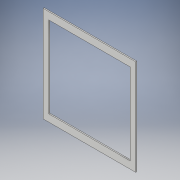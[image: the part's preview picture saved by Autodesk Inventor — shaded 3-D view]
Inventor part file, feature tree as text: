
AUTODESK INVENTOR PART (.ipt)
format: ipt  version: 2017 (Build 210142000, 142)  size: 106,496 bytes
history: native  units: in
note: dims shown in document units (in); Inventor stores cm internally (conversion verified against a paired STEP export)
features: extrude x2, sketch x2
ambient origin geometry x8: Origin, YZ Plane, XZ Plane, XY Plane, X Axis, Y Axis, Z Axis, Center Point
bodies: Solid1 (feature_tree)
feature tree (4):
  extrude  "Extrusion1"  Depth=20.0in
  extrude  "Extrusion2"  Depth=17.0in
  sketch  "Sketch1"  dims[d0=19.333in d1=20.0in]
  sketch  "Sketch2"  dims[d2=0.25in d3=0.0in d4=17.0in d5=17.0in d6=0.25in d7=0.0in]
